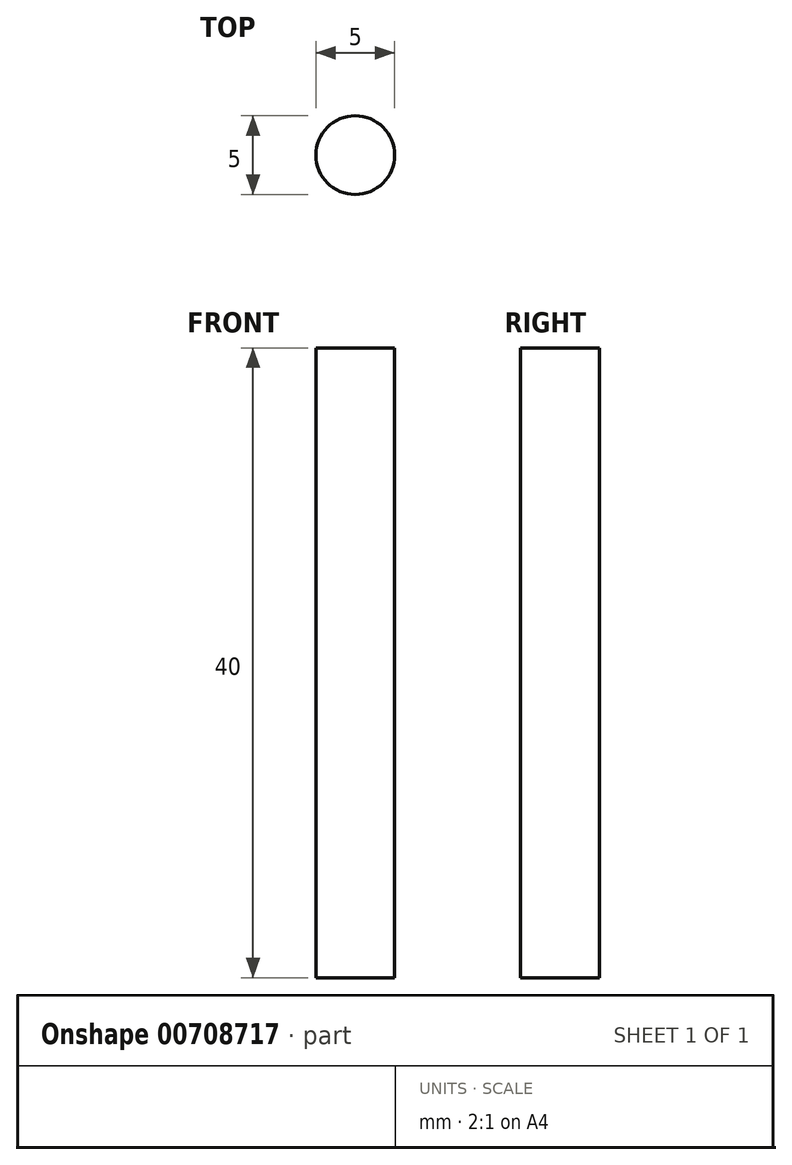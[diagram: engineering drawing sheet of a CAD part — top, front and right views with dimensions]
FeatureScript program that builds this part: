
annotation { "Feature Type Name" : "Feature", "Feature Type Description" : "" }
export const myFeature = defineFeature(function(context is Context, id is Id, definition is map)
    precondition{}
    {
        {
            var Q0;
            Q0=qCreatedBy(makeId("Top.planeOp"),FACE);
            var sketch = newSketch(context, id + "F0", { "sketchPlane" : qUnion([Q0])});
            skCircle(sketch, "E0", {"center": v(0, 0) * mm, "radius": 2.5 * mm});
            skSolve(sketch);
        }
        {
            var Q0;
            Q0 = qSketchRegion(id + "F0", true);
            var Q1;
            Q1=makeQuery(id+"F0.imprint","IMPRINT",FACE,{"disambiguationData":[TD([[makeQuery(id+"F0.imprint","IMPRINT",EDGE,{"derivedFrom":sQuery(id+"F0.wireOp",EDGE,"E0")}),1.0]])]});
            extrude(context, id + "F1", {"entities" : qUnion([Q0, Q1]), "depth" : 40 * mm, "offsetDistance" : 25 * mm});
        }
    });
